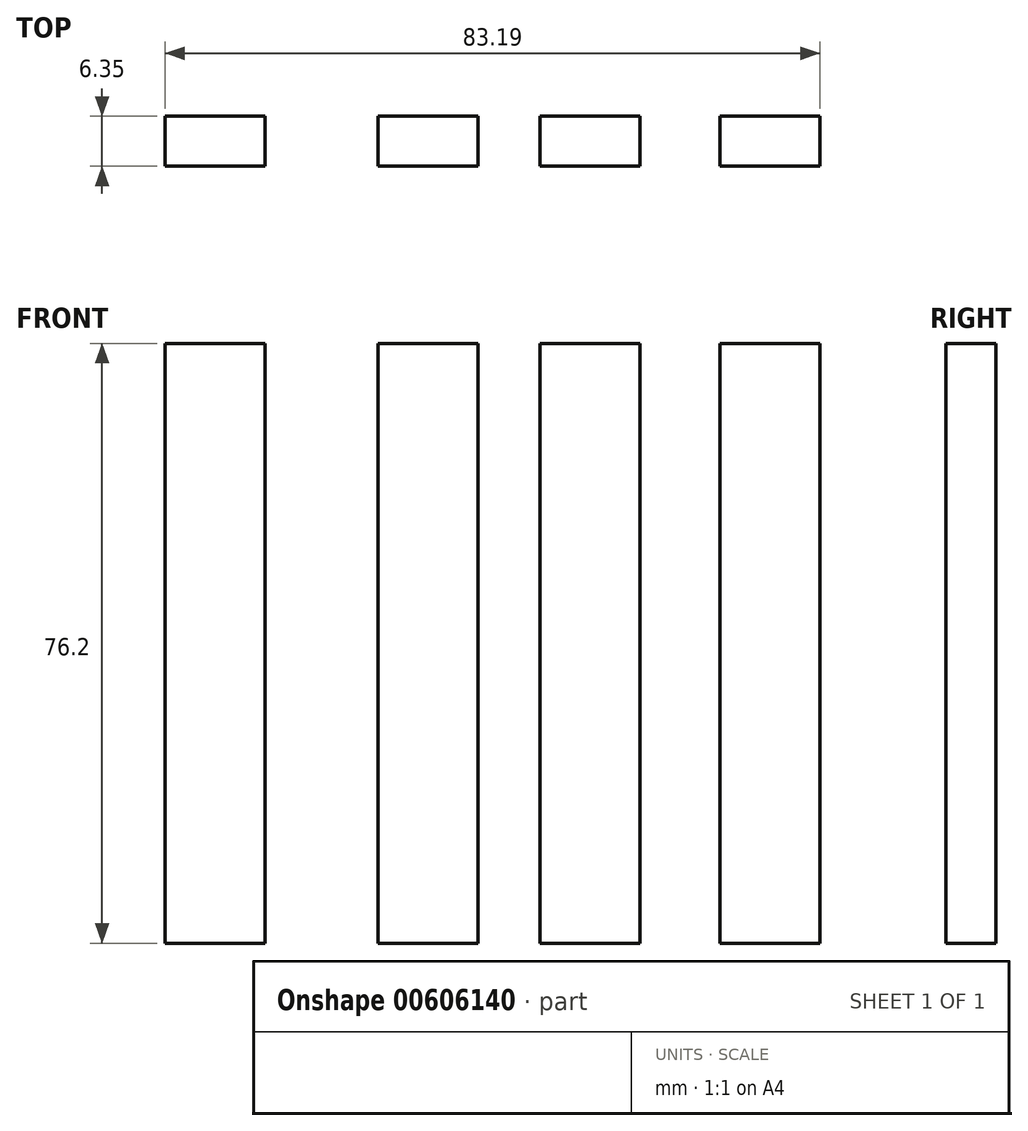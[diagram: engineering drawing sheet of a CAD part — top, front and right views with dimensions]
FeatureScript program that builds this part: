
annotation { "Feature Type Name" : "Feature", "Feature Type Description" : "" }
export const myFeature = defineFeature(function(context is Context, id is Id, definition is map)
    precondition{}
    {
        {
            var Q0;
            Q0=qCreatedBy(makeId("Front.planeOp"),FACE);
            var sketch = newSketch(context, id + "F0", { "sketchPlane" : qUnion([Q0])});
            skLineSegment(sketch, "E0.bottom", {"start": v(0, 0) * mm, "end": v(-12.7, 0) * mm});
            skLineSegment(sketch, "E0.top", {"start": v(0, 76.2) * mm, "end": v(-12.7, 76.2) * mm});
            skLineSegment(sketch, "E0.left", {"start": v(0, 0) * mm, "end": v(0, 76.2) * mm});
            skLineSegment(sketch, "E0.right", {"start": v(-12.7, 0) * mm, "end": v(-12.7, 76.2) * mm});
            skLineSegment(sketch, "E1.bottom", {"start": v(20.56, 0) * mm, "end": v(7.86, 0) * mm});
            skLineSegment(sketch, "E1.top", {"start": v(20.56, 76.2) * mm, "end": v(7.86, 76.2) * mm});
            skLineSegment(sketch, "E1.left", {"start": v(20.56, 0) * mm, "end": v(20.56, 76.2) * mm});
            skLineSegment(sketch, "E1.right", {"start": v(7.86, 0) * mm, "end": v(7.86, 76.2) * mm});
            skLineSegment(sketch, "E2.bottom", {"start": v(30.72, 0) * mm, "end": v(43.42, 0) * mm});
            skLineSegment(sketch, "E2.top", {"start": v(30.72, 76.2) * mm, "end": v(43.42, 76.2) * mm});
            skLineSegment(sketch, "E2.left", {"start": v(30.72, 0) * mm, "end": v(30.72, 76.2) * mm});
            skLineSegment(sketch, "E2.right", {"start": v(43.42, 0) * mm, "end": v(43.42, 76.2) * mm});
            skLineSegment(sketch, "E3.bottom", {"start": v(-27.07, 0) * mm, "end": v(-39.77, 0) * mm});
            skLineSegment(sketch, "E3.top", {"start": v(-27.07, 76.2) * mm, "end": v(-39.77, 76.2) * mm});
            skLineSegment(sketch, "E3.left", {"start": v(-27.07, 0) * mm, "end": v(-27.07, 76.2) * mm});
            skLineSegment(sketch, "E3.right", {"start": v(-39.77, 0) * mm, "end": v(-39.77, 76.2) * mm});
            skSolve(sketch);
        }
        {
            var Q0;
            Q0=makeQuery(id+"F0.imprint","IMPRINT",FACE,{"disambiguationData":[TD([[makeQuery(id+"F0.imprint","IMPRINT",EDGE,{"derivedFrom":sQuery(id+"F0.wireOp",EDGE,"E2.bottom")}),1.0]])]});
            var Q1;
            Q1=makeQuery(id+"F0.imprint","IMPRINT",FACE,{"disambiguationData":[TD([[makeQuery(id+"F0.imprint","IMPRINT",EDGE,{"derivedFrom":sQuery(id+"F0.wireOp",EDGE,"E1.bottom")}),-1.0]])]});
            var Q2;
            Q2=makeQuery(id+"F0.imprint","IMPRINT",FACE,{"disambiguationData":[TD([[makeQuery(id+"F0.imprint","IMPRINT",EDGE,{"derivedFrom":sQuery(id+"F0.wireOp",EDGE,"E0.bottom")}),-1.0]])]});
            var Q3;
            Q3=makeQuery(id+"F0.imprint","IMPRINT",FACE,{"disambiguationData":[TD([[makeQuery(id+"F0.imprint","IMPRINT",EDGE,{"derivedFrom":sQuery(id+"F0.wireOp",EDGE,"E3.bottom")}),-1.0]])]});
            extrude(context, id + "F1", {"entities" : qUnion([Q0, Q1, Q2, Q3]), "depth" : 6.35 * mm, "offsetDistance" : 25.4 * mm});
        }
    });
